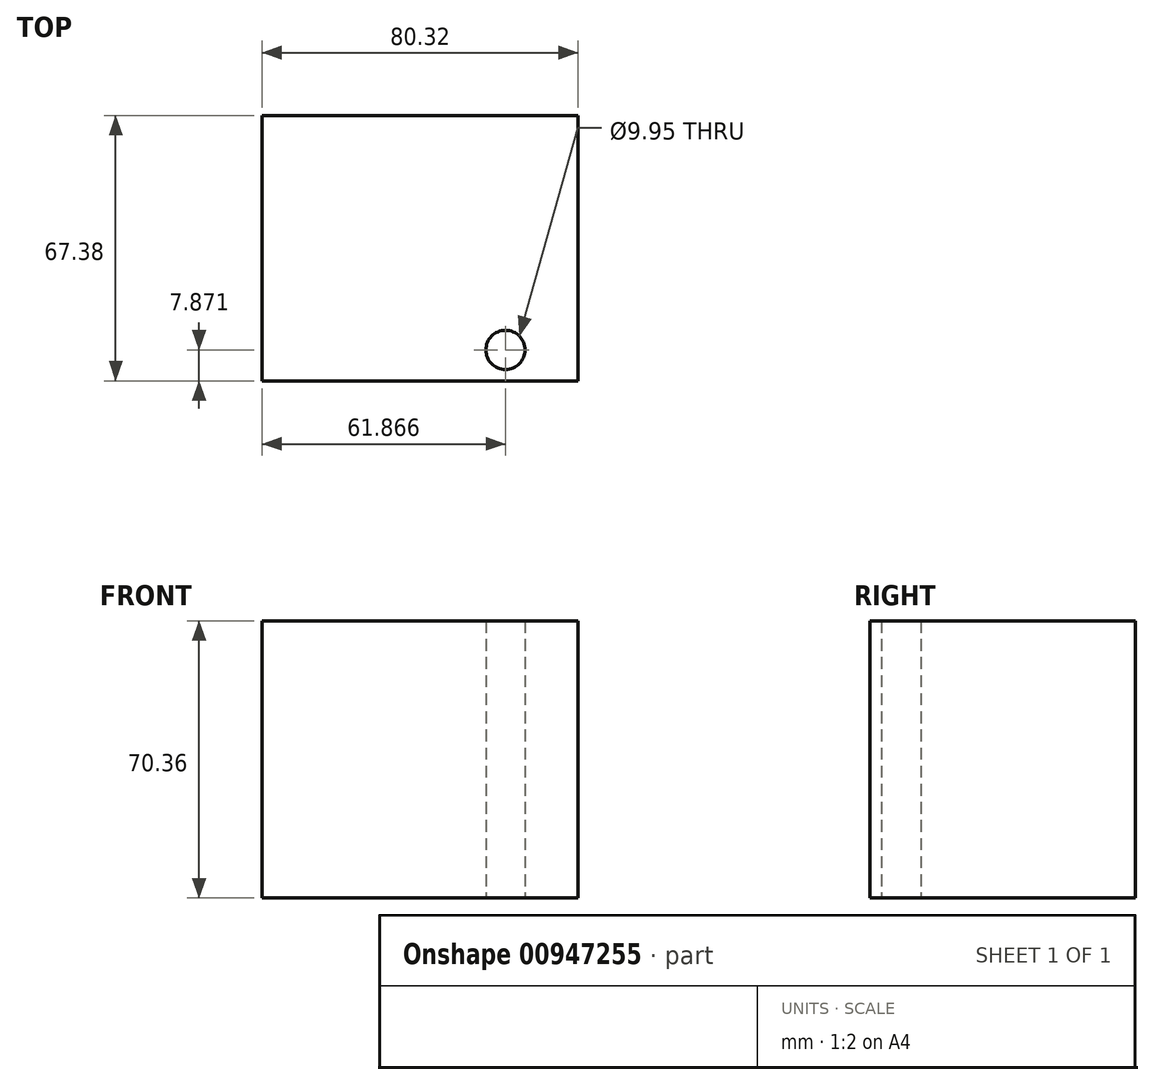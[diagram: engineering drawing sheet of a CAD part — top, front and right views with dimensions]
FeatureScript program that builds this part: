
annotation { "Feature Type Name" : "Feature", "Feature Type Description" : "" }
export const myFeature = defineFeature(function(context is Context, id is Id, definition is map)
    precondition{}
    {
        {
            var Q0;
            Q0=qCreatedBy(makeId("Top.planeOp"),FACE);
            var sketch = newSketch(context, id + "F0", { "sketchPlane" : qUnion([Q0])});
            skLineSegment(sketch, "E0.bottom", {"start": v(40.16, 33.69) * mm, "end": v(-40.16, 33.69) * mm});
            skLineSegment(sketch, "E0.top", {"start": v(40.16, -33.69) * mm, "end": v(-40.16, -33.69) * mm});
            skLineSegment(sketch, "E0.left", {"start": v(40.16, 33.69) * mm, "end": v(40.16, -33.69) * mm});
            skLineSegment(sketch, "E0.right", {"start": v(-40.16, 33.69) * mm, "end": v(-40.16, -33.69) * mm});
            skPoint(sketch, "E0.middle", {"position": v(0, 0) * mm});
            skSolve(sketch);
        }
        {
            var Q0;
            Q0=makeQuery(id+"F0.imprint","IMPRINT",FACE,{"disambiguationData":[TD([[makeQuery(id+"F0.imprint","IMPRINT",EDGE,{"derivedFrom":sQuery(id+"F0.wireOp",EDGE,"E0.bottom")}),1.0]])]});
            extrude(context, id + "F1", {"entities" : qUnion([Q0]), "oppositeDirection" : true, "depth" : 70.36 * mm, "offsetDistance" : 25.4 * mm});
        }
        {
            var Q0;
            Q0=makeQuery(id+"F1.opExtrude","CAP_FACE",FACE,{"disambiguationData":[OSD([sQuery(id+"F0.wireOp",EDGE,"E0.bottom"),sQuery(id+"F0.wireOp",EDGE,"E0.top"),sQuery(id+"F0.wireOp",EDGE,"E0.left"),sQuery(id+"F0.wireOp",EDGE,"E0.right")])],"isStart":false});
            var sketch = newSketch(context, id + "F2", { "sketchPlane" : qUnion([Q0])});
            skCircle(sketch, "E1", {"center": v(21.7, 25.82) * mm, "radius": 4.97 * mm});
            skCircle(sketch, "E2", {"center": v(21.1, 14.23) * mm, "radius": 3.34 * mm});
            skCircle(sketch, "E3", {"center": v(30.58, 5.9) * mm, "radius": 3.43 * mm});
            skCircle(sketch, "E4", {"center": v(31.42, 21.01) * mm, "radius": 3.48 * mm});
            skSolve(sketch);
        }
        {
            var Q0;
            Q0=makeQuery(id+"F2.imprint","IMPRINT",FACE,{"disambiguationData":[TD([[makeQuery(id+"F2.imprint","IMPRINT",EDGE,{"derivedFrom":sQuery(id+"F2.wireOp",EDGE,"E1")}),1.0]])]});
            var Q1;
            Q1=sQuery(id+"F2.wireOp",EDGE,"E1");
            var Q2;
            Q2=sQuery(id+"F2.wireOp",EDGE,"E4");
            var Q3;
            Q3=sQuery(id+"F2.wireOp",EDGE,"E2");
            var Q4;
            Q4=sQuery(id+"F2.wireOp",EDGE,"E3");
            extrude(context, id + "F3", {"entities" : qUnion([Q0]), "operationType" : NewBodyOperationType.REMOVE, "surfaceEntities" : qUnion([Q1, Q2, Q3, Q4]), "endBound" : BoundingType.THROUGH_ALL, "oppositeDirection" : true, "depth" : 25.4 * mm, "offsetDistance" : 25.4 * mm});
        }
    });
